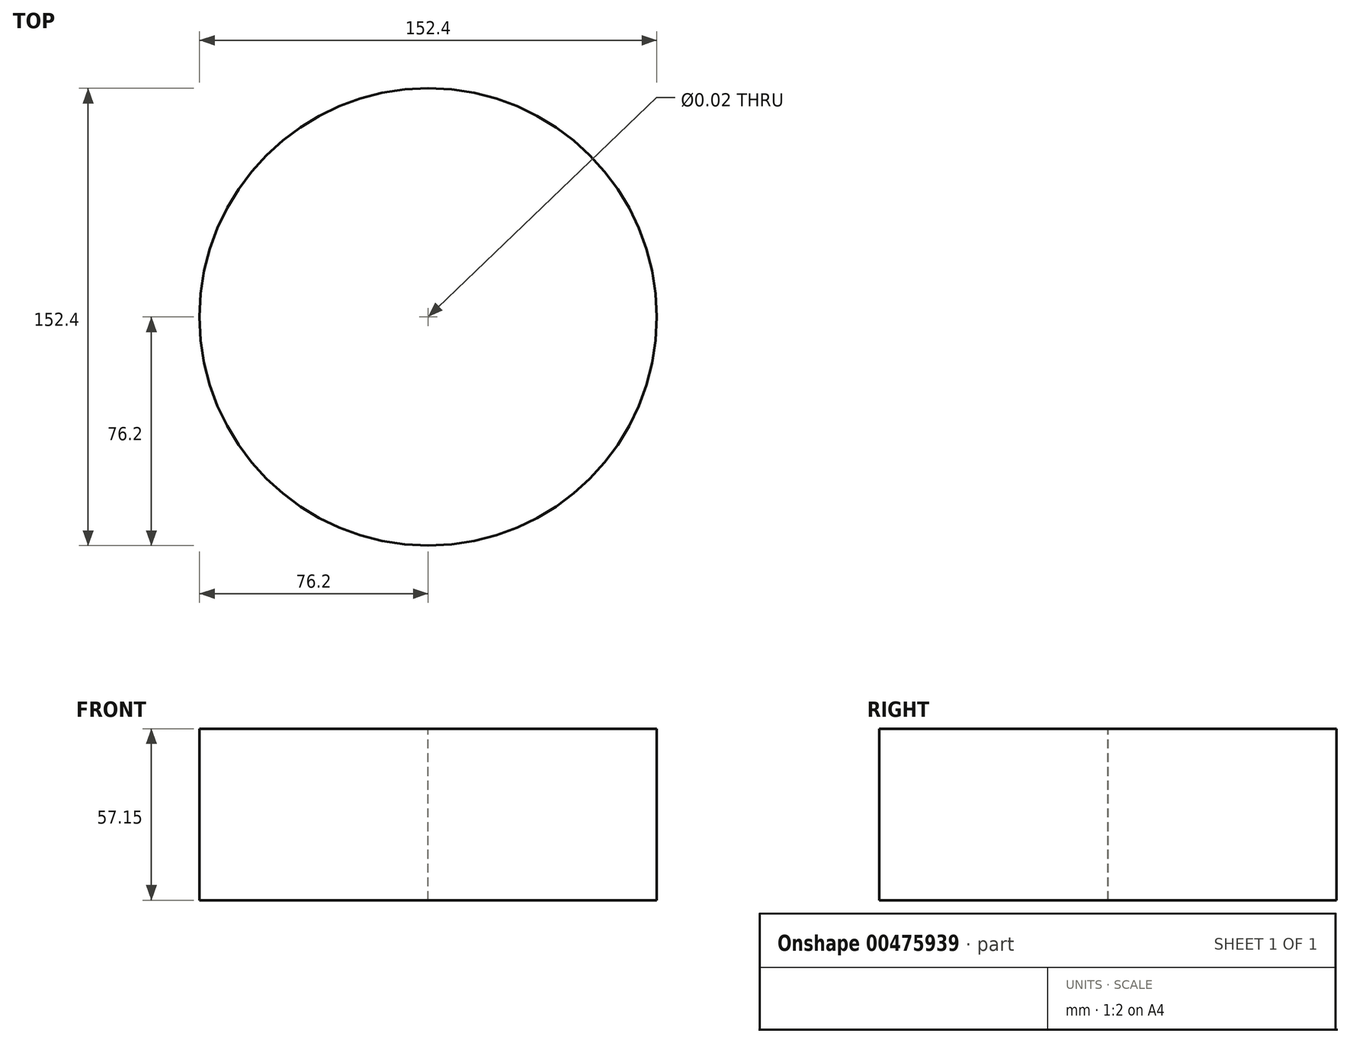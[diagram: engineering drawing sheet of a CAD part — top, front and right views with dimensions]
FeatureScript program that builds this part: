
annotation { "Feature Type Name" : "Feature", "Feature Type Description" : "" }
export const myFeature = defineFeature(function(context is Context, id is Id, definition is map)
    precondition{}
    {
        {
            var Q0;
            Q0=qCreatedBy(makeId("Top.planeOp"),FACE);
            var sketch = newSketch(context, id + "F0", { "sketchPlane" : qUnion([Q0])});
            skCircle(sketch, "E0", {"center": v(0, 0) * mm, "radius": 76.2 * mm});
            skSolve(sketch);
        }
        {
            var Q0;
            Q0=makeQuery(id+"F0.imprint","IMPRINT",FACE,{"disambiguationData":[TD([[makeQuery(id+"F0.imprint","IMPRINT",EDGE,{"derivedFrom":sQuery(id+"F0.wireOp",EDGE,"E0")}),1.0]])]});
            extrude(context, id + "F1", {"entities" : qUnion([Q0]), "depth" : 57.15 * mm});
        }
        {
            var Q0;
            Q0=makeQuery(id+"F1.opExtrude","CAP_FACE",FACE,{"disambiguationData":[OSD([sQuery(id+"F0.wireOp",EDGE,"E0")])],"isStart":false});
            var sketch = newSketch(context, id + "F2", { "sketchPlane" : qUnion([Q0])});
            skSolve(sketch);
        }
        {
            var Q0;
            Q0=makeQuery(id+"F2.imprint","IMPRINT",FACE,{"disambiguationData":[TD([[makeQuery(id+"F2.imprint","IMPRINT",EDGE,{"derivedFrom":makeQuery(id+"F1.opExtrude","CAP_EDGE",EDGE,{"disambiguationData":[OSD([sQuery(id+"F0.wireOp",EDGE,"E0")])],"isStart":false})}),1.0]])]});
            var sketch = newSketch(context, id + "F3", { "sketchPlane" : qUnion([Q0])});
            skLineSegment(sketch, "E1", {"start": v(0, 0) * mm, "end": v(510.43, -143.87) * mm});
            skSolve(sketch);
        }
        {
            var Q0;
            Q0=sQuery(id+"F3.wireOp",VERTEX,"E1.end");
            var Q1;
            Q1=sQuery(id+"F3.wireOp",VERTEX,"E1.start");
            var Q2;
            Q2=makeQuery(id+"F1.opExtrude","SWEPT_BODY",BODY,{"disambiguationData":[OSD([sQuery(id+"F0.wireOp",EDGE,"E0")])]});
            hole(context, id + "F4", {"style" : HoleStyle.SIMPLE, "endStyle" : HoleEndStyle.THROUGH, "standardTappedOrClearance" : lookupTablePath({ "standard" : "ANSI", "size" : "1/2 (0.5)", "type" : "Drilled" }), "standardBlindInLast" : lookupTablePath({ "standard" : "ANSI", "size" : "1/2", "type" : "Drilled" }), "holeDiameter" : 1 / 50.8 * mm, "isTappedThrough" : true, "tappedDepth" : 12.7 * mm, "tapClearance" : 3, "locations" : qUnion([Q0, Q1]), "scope" : qUnion([Q2])});
        }
    });
